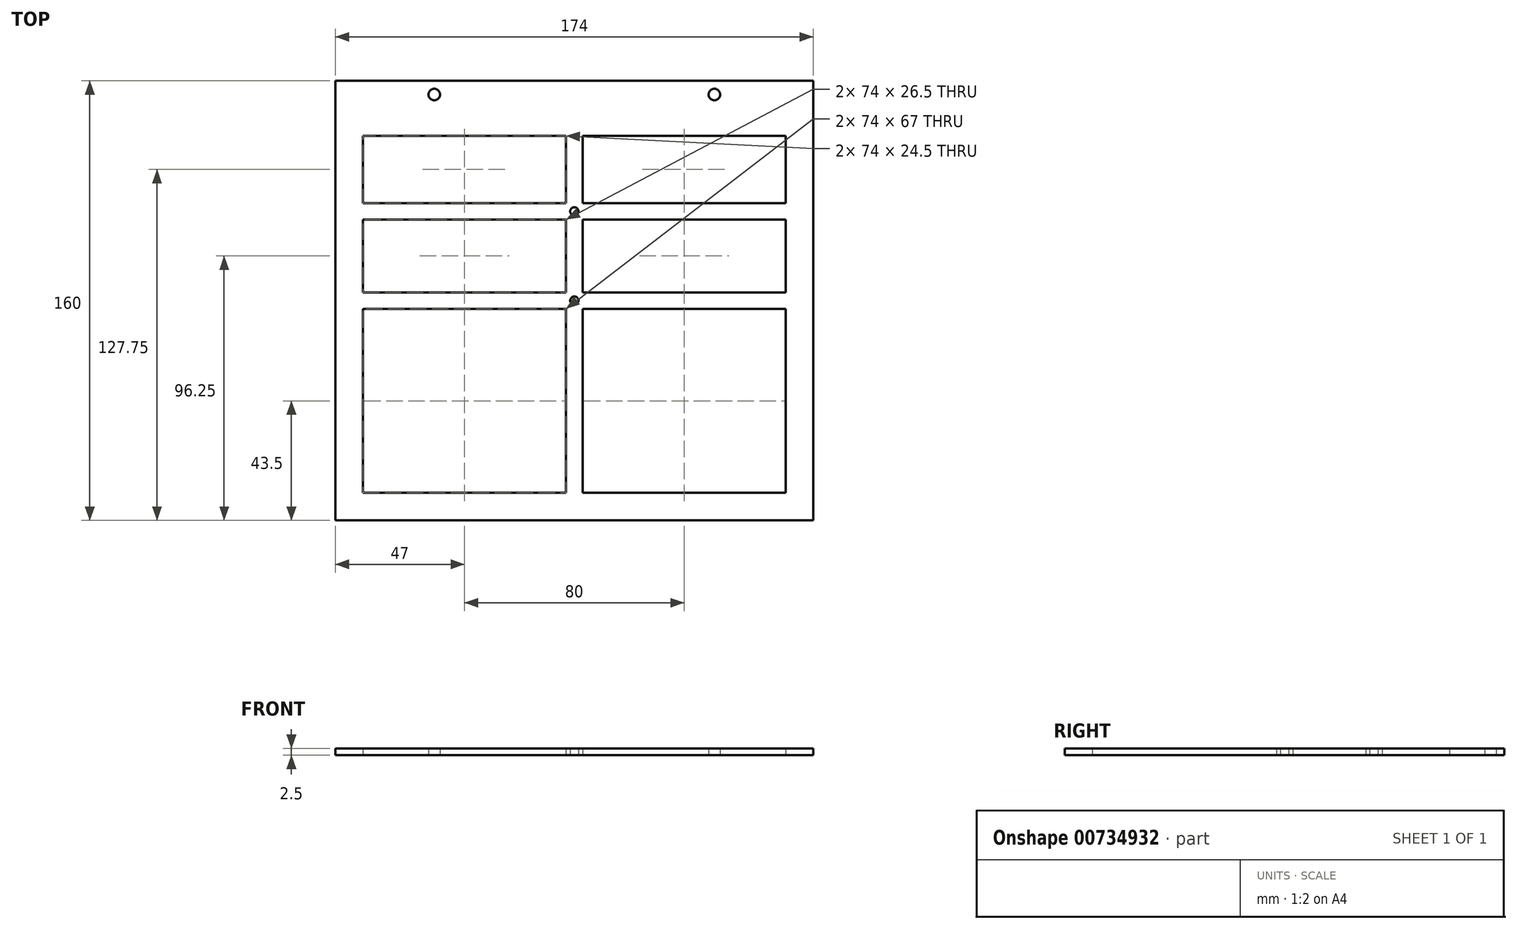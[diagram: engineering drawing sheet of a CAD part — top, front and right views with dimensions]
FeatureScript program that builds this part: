
annotation { "Feature Type Name" : "Feature", "Feature Type Description" : "" }
export const myFeature = defineFeature(function(context is Context, id is Id, definition is map)
    precondition{}
    {
        {
            var Q0;
            Q0=qCreatedBy(makeId("Top.planeOp"),FACE);
            var sketch = newSketch(context, id + "F0", { "sketchPlane" : qUnion([Q0])});
            skLineSegment(sketch, "E0.bottom", {"start": v(87, -80) * mm, "end": v(-87, -80) * mm});
            skLineSegment(sketch, "E0.top", {"start": v(87, 80) * mm, "end": v(-87, 80) * mm});
            skLineSegment(sketch, "E0.left", {"start": v(87, -80) * mm, "end": v(87, 80) * mm});
            skLineSegment(sketch, "E0.right", {"start": v(-87, -80) * mm, "end": v(-87, 80) * mm});
            skPoint(sketch, "E0.middle", {"position": v(0, 0) * mm});
            skCircle(sketch, "E1", {"center": v(-51, 75) * mm, "radius": 2.1 * mm});
            skCircle(sketch, "E2", {"center": v(51, 75) * mm, "radius": 2.1 * mm});
            skLineSegment(sketch, "E3.bottom", {"start": v(15, -23.5) * mm, "end": v(-15, -23.5) * mm, "construction": true});
            skLineSegment(sketch, "E3.top", {"start": v(15, 46.5) * mm, "end": v(-15, 46.5) * mm, "construction": true});
            skLineSegment(sketch, "E3.left", {"start": v(15, -23.5) * mm, "end": v(15, 46.5) * mm, "construction": true});
            skLineSegment(sketch, "E3.right", {"start": v(-15, -23.5) * mm, "end": v(-15, 46.5) * mm, "construction": true});
            skPoint(sketch, "E4", {"position": v(0, 46.5) * mm});
            skPoint(sketch, "E5", {"position": v(0, -23.5) * mm});
            skCircle(sketch, "E6", {"center": v(0, 32.5) * mm, "radius": 1.5 * mm});
            skCircle(sketch, "E7", {"center": v(0, 0) * mm, "radius": 1.5 * mm});
            skLineSegment(sketch, "E8", {"start": v(-87, 75) * mm, "end": v(87, 75) * mm, "construction": true});
            skLineSegment(sketch, "E9", {"start": v(-87, 70) * mm, "end": v(87, 70) * mm, "construction": true});
            skLineSegment(sketch, "E10.0", {"start": v(87, -70) * mm, "end": v(-87, -70) * mm, "construction": true});
            skLineSegment(sketch, "E11.0", {"start": v(-77, -80) * mm, "end": v(-77, 80) * mm, "construction": true});
            skLineSegment(sketch, "E12.0", {"start": v(77, -80) * mm, "end": v(77, 80) * mm, "construction": true});
            skLineSegment(sketch, "E13.0", {"start": v(-87, 60) * mm, "end": v(87, 60) * mm, "construction": true});
            skLineSegment(sketch, "E14.bottom", {"start": v(77, -70) * mm, "end": v(3, -70) * mm});
            skLineSegment(sketch, "E14.top", {"start": v(77, 60) * mm, "end": v(3, 60) * mm});
            skLineSegment(sketch, "E14.left", {"start": v(77, -70) * mm, "end": v(77, 60) * mm});
            skLineSegment(sketch, "E14.right", {"start": v(3, -70) * mm, "end": v(3, 60) * mm});
            skLineSegment(sketch, "E15.bottom", {"start": v(-77, -70) * mm, "end": v(-3, -70) * mm});
            skLineSegment(sketch, "E15.top", {"start": v(-77, 60) * mm, "end": v(-3, 60) * mm});
            skLineSegment(sketch, "E15.left", {"start": v(-77, -70) * mm, "end": v(-77, 60) * mm});
            skLineSegment(sketch, "E15.right", {"start": v(-3, -70) * mm, "end": v(-3, 60) * mm});
            skLineSegment(sketch, "E16.bottom", {"start": v(-77, 35.5) * mm, "end": v(77, 35.5) * mm});
            skLineSegment(sketch, "E16.top", {"start": v(-77, 29.5) * mm, "end": v(77, 29.5) * mm});
            skLineSegment(sketch, "E16.left", {"start": v(-77, 35.5) * mm, "end": v(-77, 29.5) * mm});
            skLineSegment(sketch, "E16.right", {"start": v(77, 35.5) * mm, "end": v(77, 29.5) * mm});
            skLineSegment(sketch, "E17.bottom", {"start": v(-77, 3) * mm, "end": v(77, 3) * mm});
            skLineSegment(sketch, "E17.top", {"start": v(-77, -3) * mm, "end": v(77, -3) * mm});
            skLineSegment(sketch, "E17.left", {"start": v(-77, 3) * mm, "end": v(-77, -3) * mm});
            skLineSegment(sketch, "E17.right", {"start": v(77, 3) * mm, "end": v(77, -3) * mm});
            skSolve(sketch);
        }
        {
            var Q0;
            Q0=makeQuery(id+"F0.imprint","IMPRINT",FACE,{"disambiguationData":[TD([[makeQuery(id+"F0.imprint","IMPRINT",EDGE,{"derivedFrom":sQuery(id+"F0.wireOp",EDGE,"E0.bottom")}),-1.0]])]});
            var Q1;
            Q1=makeQuery(id+"F0.imprint","IMPRINT",FACE,{"disambiguationData":[TD([[makeQuery(id+"F0.imprint","IMPRINT",EDGE,{"derivedFrom":sQuery(id+"F0.wireOp",EDGE,"E6")}),-1.0]])]});
            var Q2;
            {var subQ0=sQuery(id+"F0.wireOp",EDGE,"E16.top");var subQ1=sQuery(id+"F0.wireOp",EDGE,"E14.right");var subQ2=makeQuery(id+"F0.imprint","INTERSECT",VERTEX,{"derivedFrom":[subQ1,subQ0]});Q2=makeQuery(id+"F0.imprint","IMPRINT",FACE,{"disambiguationData":[TD([[makeQuery(id+"F0.imprint","IMPRINT",EDGE,{"disambiguationData":[TD([[subQ2,1.0]])],"derivedFrom":subQ1}),1.0]])]});}
            var Q3;
            Q3=makeQuery(id+"F0.imprint","IMPRINT",FACE,{"disambiguationData":[TD([[makeQuery(id+"F0.imprint","IMPRINT",EDGE,{"derivedFrom":sQuery(id+"F0.wireOp",EDGE,"E7")}),-1.0]])]});
            var Q4;
            {var subQ0=sQuery(id+"F0.wireOp",EDGE,"E17.top");var subQ1=sQuery(id+"F0.wireOp",EDGE,"E14.left");var subQ2=makeQuery(id+"F0.imprint","INTERSECT",VERTEX,{"derivedFrom":[subQ1,subQ0]});Q4=makeQuery(id+"F0.imprint","IMPRINT",FACE,{"disambiguationData":[TD([[makeQuery(id+"F0.imprint","IMPRINT",EDGE,{"disambiguationData":[TD([[subQ2,-1.0]])],"derivedFrom":subQ1}),1.0]])]});}
            var Q5;
            {var subQ0=sQuery(id+"F0.wireOp",EDGE,"E17.top");var subQ1=sQuery(id+"F0.wireOp",EDGE,"E15.left");var subQ2=makeQuery(id+"F0.imprint","INTERSECT",VERTEX,{"derivedFrom":[subQ1,subQ0]});Q5=makeQuery(id+"F0.imprint","IMPRINT",FACE,{"disambiguationData":[TD([[makeQuery(id+"F0.imprint","IMPRINT",EDGE,{"disambiguationData":[TD([[subQ2,-1.0]])],"derivedFrom":subQ1}),-1.0]])]});}
            var Q6;
            {var subQ0=sQuery(id+"F0.wireOp",EDGE,"E16.bottom");var subQ1=sQuery(id+"F0.wireOp",EDGE,"E15.left");var subQ2=makeQuery(id+"F0.imprint","INTERSECT",VERTEX,{"derivedFrom":[subQ1,subQ0]});Q6=makeQuery(id+"F0.imprint","IMPRINT",FACE,{"disambiguationData":[TD([[makeQuery(id+"F0.imprint","IMPRINT",EDGE,{"disambiguationData":[TD([[subQ2,1.0]])],"derivedFrom":subQ1}),-1.0]])]});}
            var Q7;
            {var subQ0=sQuery(id+"F0.wireOp",EDGE,"E16.bottom");var subQ1=sQuery(id+"F0.wireOp",EDGE,"E14.left");var subQ2=makeQuery(id+"F0.imprint","INTERSECT",VERTEX,{"derivedFrom":[subQ1,subQ0]});Q7=makeQuery(id+"F0.imprint","IMPRINT",FACE,{"disambiguationData":[TD([[makeQuery(id+"F0.imprint","IMPRINT",EDGE,{"disambiguationData":[TD([[subQ2,1.0]])],"derivedFrom":subQ1}),1.0]])]});}
            extrude(context, id + "F1", {"entities" : qUnion([Q0, Q1, Q2, Q3, Q4, Q5, Q6, Q7]), "depth" : 2.5 * mm, "offsetDistance" : 25 * mm});
        }
    });
